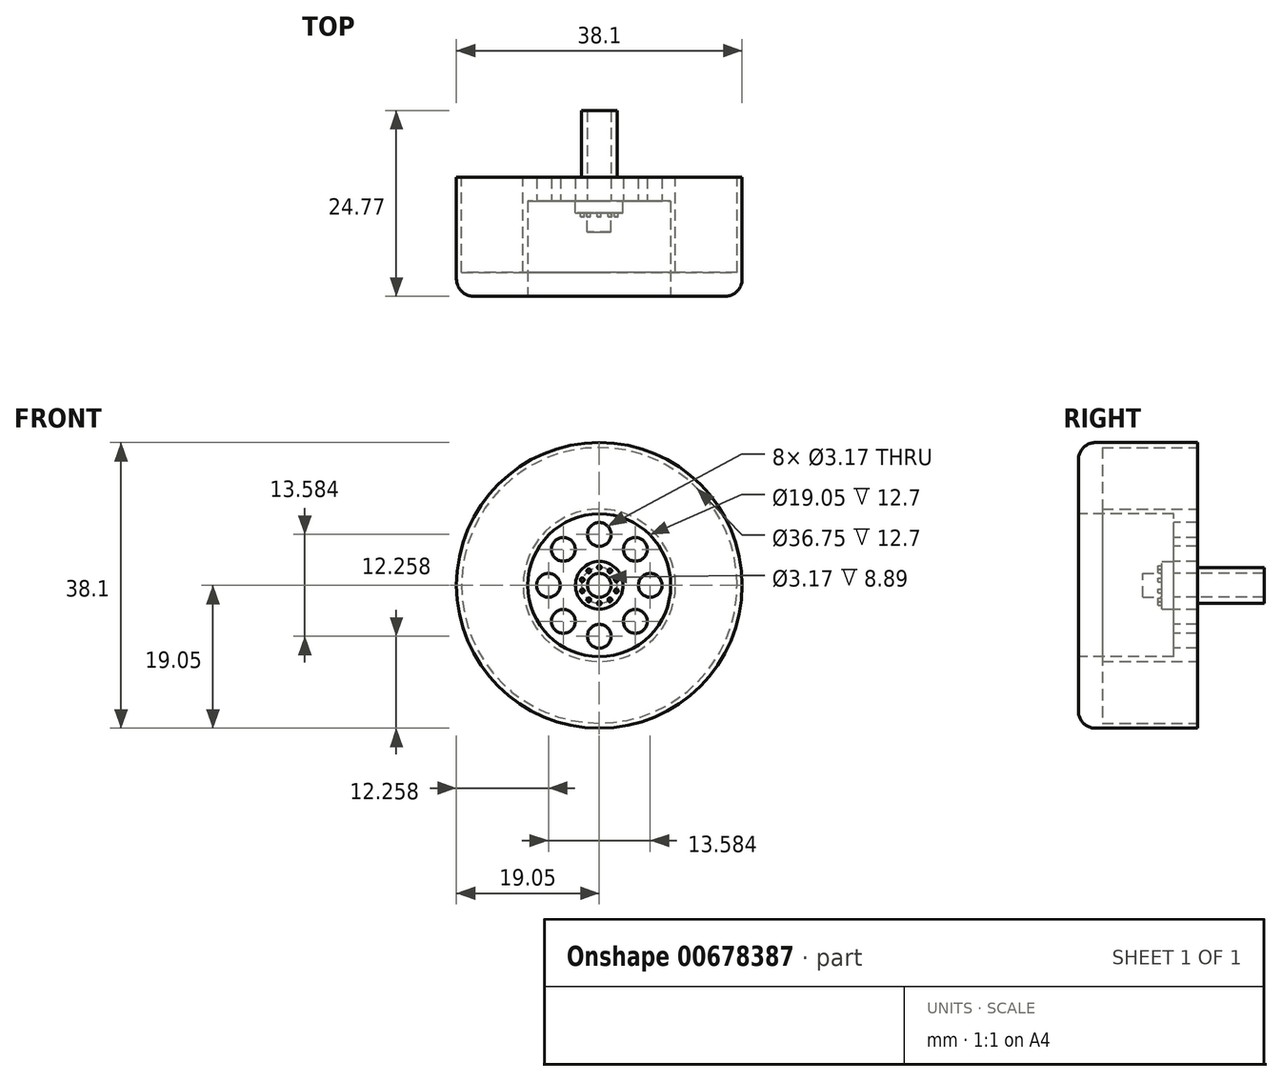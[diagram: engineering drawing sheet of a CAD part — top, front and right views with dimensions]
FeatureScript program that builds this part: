
annotation { "Feature Type Name" : "Feature", "Feature Type Description" : "" }
export const myFeature = defineFeature(function(context is Context, id is Id, definition is map)
    precondition{}
    {
        {
            var Q0;
            Q0=qCreatedBy(makeId("Front.planeOp"),FACE);
            var sketch = newSketch(context, id + "F0", { "sketchPlane" : qUnion([Q0])});
            skCircle(sketch, "E0", {"center": v(0, 0) * mm, "radius": 19.05 * mm});
            skSolve(sketch);
        }
        {
            var Q0;
            Q0=makeQuery(id+"F0.imprint","IMPRINT",FACE,{"disambiguationData":[TD([[makeQuery(id+"F0.imprint","IMPRINT",EDGE,{"derivedFrom":sQuery(id+"F0.wireOp",EDGE,"E0")}),1.0]])]});
            extrude(context, id + "F1", {"entities" : qUnion([Q0]), "depth" : 15.88 * mm, "offsetDistance" : 25.4 * mm});
        }
        {
            var Q0;
            Q0=makeQuery(id+"F1.opExtrude","CAP_FACE",FACE,{"disambiguationData":[OSD([sQuery(id+"F0.wireOp",EDGE,"E0")])],"isStart":false});
            var sketch = newSketch(context, id + "F2", { "sketchPlane" : qUnion([Q0])});
            skCircle(sketch, "E1", {"center": v(0, 0) * mm, "radius": 9.53 * mm});
            skSolve(sketch);
        }
        {
            var Q0;
            Q0=makeQuery(id+"F2.imprint","IMPRINT",FACE,{"disambiguationData":[TD([[makeQuery(id+"F2.imprint","IMPRINT",EDGE,{"derivedFrom":sQuery(id+"F2.wireOp",EDGE,"E1")}),1.0]])]});
            extrude(context, id + "F3", {"entities" : qUnion([Q0]), "operationType" : NewBodyOperationType.REMOVE, "oppositeDirection" : true, "depth" : 12.7 * mm, "offsetDistance" : 25.4 * mm});
        }
        {
            var Q0;
            Q0=makeQuery(id+"F1.opExtrude","CAP_FACE",FACE,{"disambiguationData":[OSD([sQuery(id+"F0.wireOp",EDGE,"E0")])],"isStart":true});
            var sketch = newSketch(context, id + "F4", { "sketchPlane" : qUnion([Q0])});
            skCircle(sketch, "E2", {"center": v(0, 0) * mm, "radius": 10.16 * mm});
            skCircle(sketch, "E3", {"center": v(0, 0) * mm, "radius": 18.38 * mm});
            skSolve(sketch);
        }
        {
            var Q0;
            Q0=makeQuery(id+"F4.imprint","IMPRINT",FACE,{"disambiguationData":[TD([[makeQuery(id+"F4.imprint","IMPRINT",EDGE,{"derivedFrom":sQuery(id+"F4.wireOp",EDGE,"E2")}),-1.0]])]});
            extrude(context, id + "F5", {"entities" : qUnion([Q0]), "operationType" : NewBodyOperationType.REMOVE, "oppositeDirection" : true, "depth" : 12.7 * mm, "offsetDistance" : 25.4 * mm});
        }
        {
            var Q0;
            Q0=makeQuery(id+"F3.boolean.opBoolean","COPY",FACE,{"derivedFrom":makeQuery(id+"F3.opExtrude","CAP_FACE",FACE,{"disambiguationData":[OSD([sQuery(id+"F2.wireOp",EDGE,"E1")])],"isStart":false})});
            var sketch = newSketch(context, id + "F6", { "sketchPlane" : qUnion([Q0])});
            skLineSegment(sketch, "E4", {"start": v(0, 0) * mm, "end": v(0, 8.09) * mm});
            skCircle(sketch, "E5", {"center": v(0, 6.8) * mm, "radius": 1.59 * mm});
            skCircle(sketch, "E6.1.0", {"center": v(-4.8, 4.8) * mm, "radius": 1.59 * mm});
            skCircle(sketch, "E6.2.0", {"center": v(-6.8, 0) * mm, "radius": 1.59 * mm});
            skCircle(sketch, "E6.3.0", {"center": v(-4.8, -4.8) * mm, "radius": 1.59 * mm});
            skCircle(sketch, "E6.4.0", {"center": v(0, -6.8) * mm, "radius": 1.59 * mm});
            skCircle(sketch, "E6.5.0", {"center": v(4.8, -4.8) * mm, "radius": 1.59 * mm});
            skCircle(sketch, "E6.6.0", {"center": v(6.8, 0) * mm, "radius": 1.59 * mm});
            skCircle(sketch, "E6.7.0", {"center": v(4.8, 4.8) * mm, "radius": 1.59 * mm});
            skPoint(sketch, "E6.center", {"position": v(0, 0) * mm});
            skSolve(sketch);
        }
        {
            var Q0;
            Q0=makeQuery(id+"F6.imprint","IMPRINT",FACE,{"disambiguationData":[TD([[makeQuery(id+"F6.imprint","IMPRINT",EDGE,{"derivedFrom":sQuery(id+"F6.wireOp",EDGE,"E5")}),1.0]])]});
            var Q1;
            Q1=makeQuery(id+"F6.imprint","IMPRINT",FACE,{"disambiguationData":[TD([[makeQuery(id+"F6.imprint","IMPRINT",EDGE,{"derivedFrom":sQuery(id+"F6.wireOp",EDGE,"E6.1.0")}),1.0]])]});
            var Q2;
            Q2=makeQuery(id+"F6.imprint","IMPRINT",FACE,{"disambiguationData":[TD([[makeQuery(id+"F6.imprint","IMPRINT",EDGE,{"derivedFrom":sQuery(id+"F6.wireOp",EDGE,"E6.2.0")}),1.0]])]});
            var Q3;
            Q3=makeQuery(id+"F6.imprint","IMPRINT",FACE,{"disambiguationData":[TD([[makeQuery(id+"F6.imprint","IMPRINT",EDGE,{"derivedFrom":sQuery(id+"F6.wireOp",EDGE,"E6.3.0")}),1.0]])]});
            var Q4;
            Q4=makeQuery(id+"F6.imprint","IMPRINT",FACE,{"disambiguationData":[TD([[makeQuery(id+"F6.imprint","IMPRINT",EDGE,{"derivedFrom":sQuery(id+"F6.wireOp",EDGE,"E6.4.0")}),1.0]])]});
            var Q5;
            Q5=makeQuery(id+"F6.imprint","IMPRINT",FACE,{"disambiguationData":[TD([[makeQuery(id+"F6.imprint","IMPRINT",EDGE,{"derivedFrom":sQuery(id+"F6.wireOp",EDGE,"E6.5.0")}),1.0]])]});
            var Q6;
            Q6=makeQuery(id+"F6.imprint","IMPRINT",FACE,{"disambiguationData":[TD([[makeQuery(id+"F6.imprint","IMPRINT",EDGE,{"derivedFrom":sQuery(id+"F6.wireOp",EDGE,"E6.6.0")}),1.0]])]});
            var Q7;
            Q7=makeQuery(id+"F6.imprint","IMPRINT",FACE,{"disambiguationData":[TD([[makeQuery(id+"F6.imprint","IMPRINT",EDGE,{"derivedFrom":sQuery(id+"F6.wireOp",EDGE,"E6.7.0")}),1.0]])]});
            extrude(context, id + "F7", {"entities" : qUnion([Q0, Q1, Q2, Q3, Q4, Q5, Q6, Q7]), "operationType" : NewBodyOperationType.REMOVE, "oppositeDirection" : true, "depth" : 25.4 * mm, "offsetDistance" : 25.4 * mm});
        }
        {
            var Q0;
            Q0=makeQuery(id+"F3.boolean.opBoolean","COPY",FACE,{"derivedFrom":makeQuery(id+"F3.opExtrude","CAP_FACE",FACE,{"disambiguationData":[OSD([sQuery(id+"F2.wireOp",EDGE,"E1")])],"isStart":false})});
            var sketch = newSketch(context, id + "F8", { "sketchPlane" : qUnion([Q0])});
            skCircle(sketch, "E7", {"center": v(0, 0) * mm, "radius": 3.17 * mm});
            skSolve(sketch);
        }
        {
            var Q0;
            Q0=makeQuery(id+"F8.imprint","IMPRINT",FACE,{"disambiguationData":[TD([[makeQuery(id+"F8.imprint","IMPRINT",EDGE,{"derivedFrom":sQuery(id+"F8.wireOp",EDGE,"E7")}),1.0]])]});
            extrude(context, id + "F9", {"entities" : qUnion([Q0]), "operationType" : NewBodyOperationType.ADD, "depth" : 1.59 * mm, "offsetDistance" : 25.4 * mm});
        }
        {
            var Q0;
            Q0=makeQuery(id+"F9.opExtrude","CAP_FACE",FACE,{"disambiguationData":[OSD([sQuery(id+"F8.wireOp",EDGE,"E7")])],"isStart":false});
            var sketch = newSketch(context, id + "F10", { "sketchPlane" : qUnion([Q0])});
            skCircle(sketch, "E8", {"center": v(0, 0) * mm, "radius": 1.59 * mm});
            skSolve(sketch);
        }
        {
            var Q0;
            Q0=makeQuery(id+"F10.imprint","IMPRINT",FACE,{"disambiguationData":[TD([[makeQuery(id+"F10.imprint","IMPRINT",EDGE,{"derivedFrom":sQuery(id+"F10.wireOp",EDGE,"E8")}),1.0]])]});
            extrude(context, id + "F11", {"entities" : qUnion([Q0]), "operationType" : NewBodyOperationType.ADD, "depth" : 2.54 * mm, "offsetDistance" : 25.4 * mm});
        }
        {
            var Q0;
            Q0=makeQuery(id+"F9.opExtrude","CAP_FACE",FACE,{"disambiguationData":[OSD([sQuery(id+"F8.wireOp",EDGE,"E7")])],"isStart":false});
            var sketch = newSketch(context, id + "F12", { "sketchPlane" : qUnion([Q0])});
            skLineSegment(sketch, "E9", {"start": v(0, 0) * mm, "end": v(0, 2.9) * mm});
            skCircle(sketch, "E10", {"center": v(0, 2.4) * mm, "radius": 0.25 * mm});
            skCircle(sketch, "E11.1.0", {"center": v(-1.4, 1.93) * mm, "radius": 0.25 * mm});
            skCircle(sketch, "E11.2.0", {"center": v(-2.27, 0.74) * mm, "radius": 0.25 * mm});
            skCircle(sketch, "E11.3.0", {"center": v(-2.27, -0.74) * mm, "radius": 0.25 * mm});
            skCircle(sketch, "E11.4.0", {"center": v(-1.4, -1.93) * mm, "radius": 0.25 * mm});
            skCircle(sketch, "E11.5.0", {"center": v(0, -2.4) * mm, "radius": 0.25 * mm});
            skCircle(sketch, "E11.6.0", {"center": v(1.4, -1.93) * mm, "radius": 0.25 * mm});
            skCircle(sketch, "E11.7.0", {"center": v(2.27, -0.74) * mm, "radius": 0.25 * mm});
            skCircle(sketch, "E11.8.0", {"center": v(2.27, 0.74) * mm, "radius": 0.25 * mm});
            skCircle(sketch, "E11.9.0", {"center": v(1.4, 1.93) * mm, "radius": 0.25 * mm});
            skPoint(sketch, "E11.center", {"position": v(0, 0) * mm});
            skSolve(sketch);
        }
        {
            var Q0;
            {var subQ0=sQuery(id+"F12.wireOp",EDGE,"E10");var subQ1=sQuery(id+"F12.wireOp",EDGE,"E9");var subQ2=makeQuery(id+"F12.imprint","INTERSECT",VERTEX,{"disambiguationData":[OD(0.0)],"derivedFrom":[subQ1,subQ0]});Q0=makeQuery(id+"F12.imprint","IMPRINT",FACE,{"disambiguationData":[TD([[makeQuery(id+"F12.imprint","IMPRINT",EDGE,{"disambiguationData":[TD([[subQ2,-1.0]])],"derivedFrom":subQ1}),1.0]])]});}
            var Q1;
            {var subQ0=sQuery(id+"F12.wireOp",EDGE,"E10");var subQ1=sQuery(id+"F12.wireOp",EDGE,"E9");var subQ2=makeQuery(id+"F12.imprint","INTERSECT",VERTEX,{"disambiguationData":[OD(0.0)],"derivedFrom":[subQ1,subQ0]});Q1=makeQuery(id+"F12.imprint","IMPRINT",FACE,{"disambiguationData":[TD([[makeQuery(id+"F12.imprint","IMPRINT",EDGE,{"disambiguationData":[TD([[subQ2,-1.0]])],"derivedFrom":subQ1}),-1.0]])]});}
            var Q2;
            Q2=makeQuery(id+"F12.imprint","IMPRINT",FACE,{"disambiguationData":[TD([[makeQuery(id+"F12.imprint","IMPRINT",EDGE,{"derivedFrom":sQuery(id+"F12.wireOp",EDGE,"E11.9.0")}),1.0]])]});
            var Q3;
            Q3=makeQuery(id+"F12.imprint","IMPRINT",FACE,{"disambiguationData":[TD([[makeQuery(id+"F12.imprint","IMPRINT",EDGE,{"derivedFrom":sQuery(id+"F12.wireOp",EDGE,"E11.8.0")}),1.0]])]});
            var Q4;
            Q4=makeQuery(id+"F12.imprint","IMPRINT",FACE,{"disambiguationData":[TD([[makeQuery(id+"F12.imprint","IMPRINT",EDGE,{"derivedFrom":sQuery(id+"F12.wireOp",EDGE,"E11.7.0")}),1.0]])]});
            var Q5;
            Q5=makeQuery(id+"F12.imprint","IMPRINT",FACE,{"disambiguationData":[TD([[makeQuery(id+"F12.imprint","IMPRINT",EDGE,{"derivedFrom":sQuery(id+"F12.wireOp",EDGE,"E11.5.0")}),1.0]])]});
            var Q6;
            Q6=makeQuery(id+"F12.imprint","IMPRINT",FACE,{"disambiguationData":[TD([[makeQuery(id+"F12.imprint","IMPRINT",EDGE,{"derivedFrom":sQuery(id+"F12.wireOp",EDGE,"E11.4.0")}),1.0]])]});
            var Q7;
            Q7=makeQuery(id+"F12.imprint","IMPRINT",FACE,{"disambiguationData":[TD([[makeQuery(id+"F12.imprint","IMPRINT",EDGE,{"derivedFrom":sQuery(id+"F12.wireOp",EDGE,"E11.6.0")}),1.0]])]});
            var Q8;
            Q8=makeQuery(id+"F12.imprint","IMPRINT",FACE,{"disambiguationData":[TD([[makeQuery(id+"F12.imprint","IMPRINT",EDGE,{"derivedFrom":sQuery(id+"F12.wireOp",EDGE,"E11.2.0")}),1.0]])]});
            var Q9;
            Q9=makeQuery(id+"F12.imprint","IMPRINT",FACE,{"disambiguationData":[TD([[makeQuery(id+"F12.imprint","IMPRINT",EDGE,{"derivedFrom":sQuery(id+"F12.wireOp",EDGE,"E11.1.0")}),1.0]])]});
            var Q10;
            Q10=makeQuery(id+"F12.imprint","IMPRINT",FACE,{"disambiguationData":[TD([[makeQuery(id+"F12.imprint","IMPRINT",EDGE,{"derivedFrom":sQuery(id+"F12.wireOp",EDGE,"E11.3.0")}),1.0]])]});
            extrude(context, id + "F13", {"entities" : qUnion([Q0, Q1, Q2, Q3, Q4, Q5, Q6, Q7, Q8, Q9, Q10]), "operationType" : NewBodyOperationType.ADD, "depth" : 0.5 * mm, "offsetDistance" : 25.4 * mm});
        }
        {
            var Q0;
            Q0=makeQuery(id+"F5.boolean.opBoolean","SPLIT",FACE,{"disambiguationData":[TD([makeQuery(id+"F5.opExtrude","SWEPT_FACE",FACE,{"disambiguationData":[OSD([sQuery(id+"F4.wireOp",EDGE,"E2")])]})])],"derivedFrom":makeQuery(id+"F1.opExtrude","CAP_FACE",FACE,{"disambiguationData":[OSD([sQuery(id+"F0.wireOp",EDGE,"E0")])],"isStart":true})});
            var sketch = newSketch(context, id + "F14", { "sketchPlane" : qUnion([Q0])});
            skCircle(sketch, "E12", {"center": v(0, 0) * mm, "radius": 2.38 * mm});
            skCircle(sketch, "E13", {"center": v(0, 0) * mm, "radius": 1.59 * mm});
            skSolve(sketch);
        }
        {
            var Q0;
            Q0=makeQuery(id+"F14.imprint","IMPRINT",FACE,{"disambiguationData":[TD([[makeQuery(id+"F14.imprint","IMPRINT",EDGE,{"derivedFrom":sQuery(id+"F14.wireOp",EDGE,"E12")}),1.0]])]});
            extrude(context, id + "F15", {"entities" : qUnion([Q0]), "operationType" : NewBodyOperationType.ADD, "depth" : 8.9 * mm, "offsetDistance" : 25.4 * mm});
        }
        {
            var Q0;
            Q0=makeQuery(id+"F1.opExtrude","CAP_EDGE",EDGE,{"disambiguationData":[OSD([sQuery(id+"F0.wireOp",EDGE,"E0")])],"isStart":false});
            fillet(context, id + "F16", {"entities" : qUnion([Q0]), "radius" : 2.3 * mm, "tangentPropagation" : true, "allowEdgeOverflow" : false});
        }
    });
